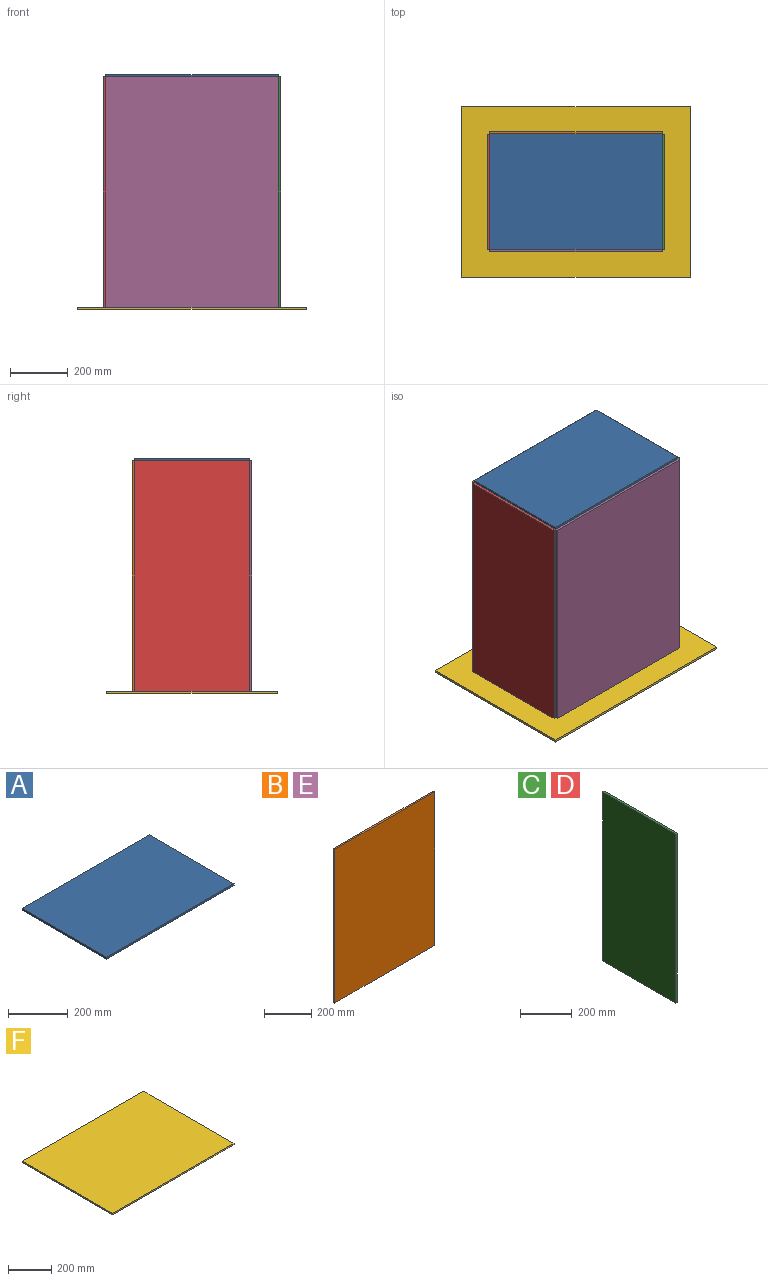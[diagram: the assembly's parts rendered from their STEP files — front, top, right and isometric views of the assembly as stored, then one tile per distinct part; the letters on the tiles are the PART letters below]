
ASSEMBLY  parts=6 mates=5
PART A: 6 faces, bbox 600x400x8 mm
  f0: plane 400x8mm, normal (-1,0,0), area 3200mm2, adj f1,f3,f4,f5
  f1: plane 600x8mm, normal (0,-1,0), area 4800mm2, adj f0,f2,f4,f5
  f2: plane 400x8mm, normal (1,0,0), area 3200mm2, adj f1,f3,f4,f5
  f3: plane 600x8mm, normal (0,1,0), area 4800mm2, adj f0,f2,f4,f5
  f4: plane 600x400mm, normal (0,0,1), area 240000mm2, adj f0,f1,f2,f3
  f5: plane 600x400mm, normal (0,0,-1), area 240000mm2, adj f0,f1,f2,f3
PART B: 6 faces, bbox 600x8x800 mm
  f0: plane 800x8mm, normal (-1,0,0), area 6400mm2, adj f1,f3,f4,f5
  f1: plane 600x8mm, normal (0,0,-1), area 4800mm2, adj f0,f2,f4,f5
  f2: plane 800x8mm, normal (1,0,0), area 6400mm2, adj f1,f3,f4,f5
  f3: plane 600x8mm, normal (0,0,1), area 4800mm2, adj f0,f2,f4,f5
  f4: plane 800x600mm, normal (0,-1,0), area 480000mm2, adj f0,f1,f2,f3
  f5: plane 800x600mm, normal (0,1,0), area 480000mm2, adj f0,f1,f2,f3
PART C: 6 faces, bbox 8x400x800 mm
  f0: plane 800x8mm, normal (0,-1,0), area 6400mm2, adj f1,f3,f4,f5
  f1: plane 400x8mm, normal (0,0,-1), area 3200mm2, adj f0,f2,f4,f5
  f2: plane 800x8mm, normal (0,1,0), area 6400mm2, adj f1,f3,f4,f5
  f3: plane 400x8mm, normal (0,0,1), area 3200mm2, adj f0,f2,f4,f5
  f4: plane 800x400mm, normal (1,0,0), area 320000mm2, adj f0,f1,f2,f3
  f5: plane 800x400mm, normal (-1,0,0), area 320000mm2, adj f0,f1,f2,f3
PART D: same geometry as C
PART E: same geometry as B
PART F: 6 faces, bbox 792x592x8 mm
  f0: plane 592x8mm, normal (-1,0,0), area 4736mm2, adj f1,f3,f4,f5
  f1: plane 792x8mm, normal (0,-1,0), area 6336mm2, adj f0,f2,f4,f5
  f2: plane 592x8mm, normal (1,0,0), area 4736mm2, adj f1,f3,f4,f5
  f3: plane 792x8mm, normal (0,1,0), area 6336mm2, adj f0,f2,f4,f5
  f4: plane 792x592mm, normal (0,0,1), area 468864mm2, adj f0,f1,f2,f3
  f5: plane 792x592mm, normal (0,0,-1), area 468864mm2, adj f0,f1,f2,f3
PLACE A t=(0,0,808)mm
PLACE B t=(0,204,404)mm
PLACE C t=(304,0,404)mm
PLACE D t=(-304,0,404)mm
PLACE E t=(0,-204,404)mm
PLACE F at identity fixed
MATE fastened A.f5 <-> B.f3  axis (0,0,-1) through (0,200,804)mm
MATE fastened B.f1 <-> F.f4  axis (0,0,-1) through (0,204,4)mm
MATE fastened D.f1 <-> B.f1  axis (0,0,-1) through (-300,200,4)mm
MATE fastened E.f1 <-> C.f1  axis (0,0,-1) through (300,-200,4)mm
MATE fastened C.f1 <-> B.f1  axis (0,0,-1) through (300,200,4)mm
